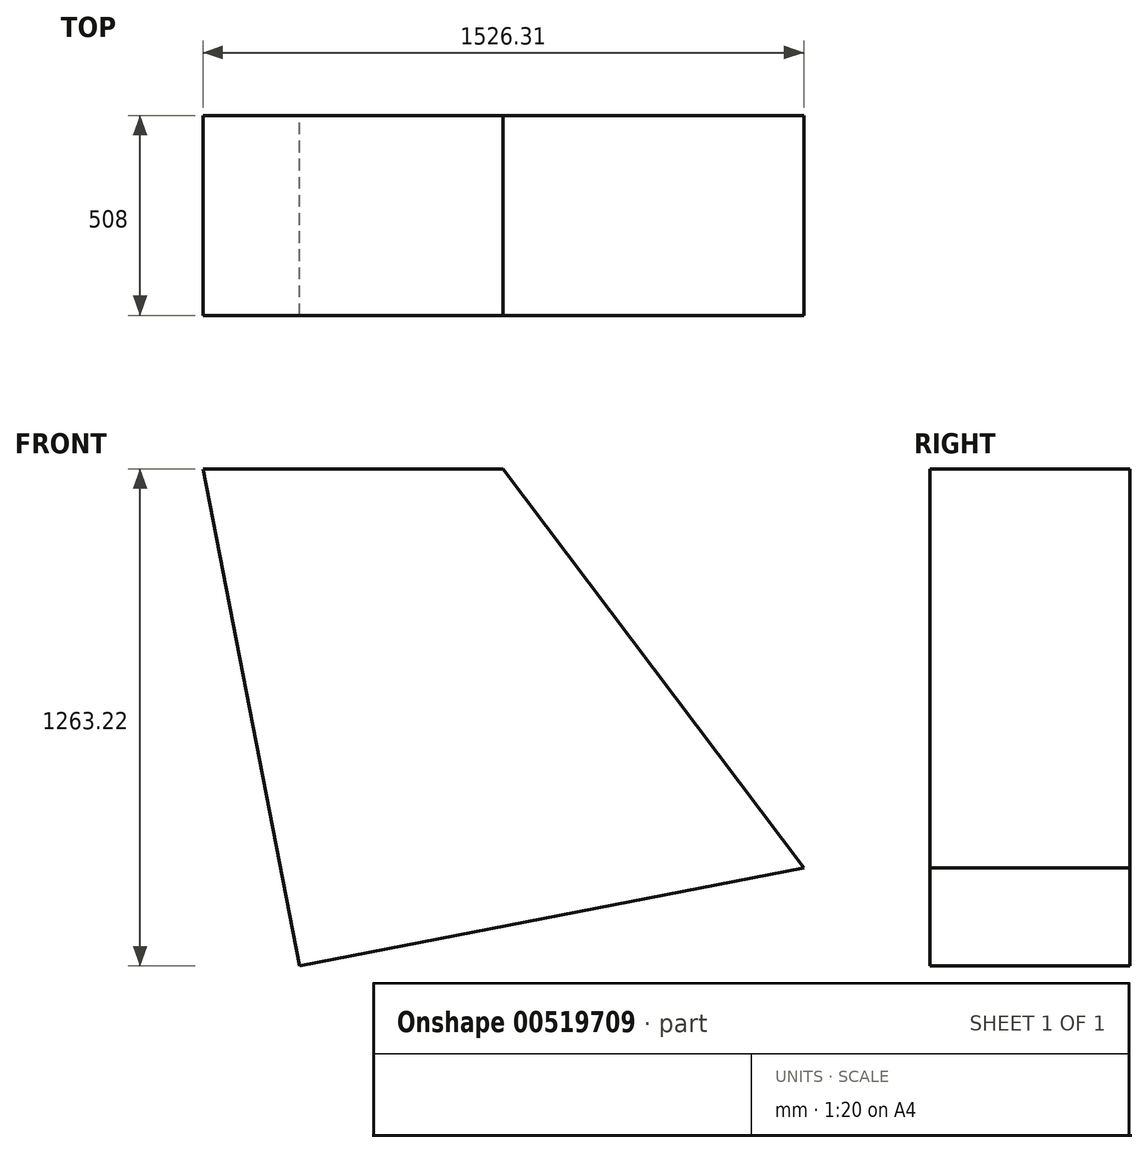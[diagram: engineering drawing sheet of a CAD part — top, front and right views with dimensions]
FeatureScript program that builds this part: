
annotation { "Feature Type Name" : "Feature", "Feature Type Description" : "" }
export const myFeature = defineFeature(function(context is Context, id is Id, definition is map)
    precondition{}
    {
        {
            var Q0;
            Q0=qCreatedBy(makeId("Front.planeOp"),FACE);
            var sketch = newSketch(context, id + "F0", { "sketchPlane" : qUnion([Q0])});
            skLineSegment(sketch, "E0", {"start": v(0, 53.86) * mm, "end": v(245.55, -1209.36) * mm});
            skLineSegment(sketch, "E1", {"start": v(0, 53.86) * mm, "end": v(762, 53.86) * mm});
            skLineSegment(sketch, "E2", {"start": v(762, 53.86) * mm, "end": v(1526.3, -960.4) * mm});
            skLineSegment(sketch, "E3", {"start": v(245.55, -1209.36) * mm, "end": v(1526.3, -960.4) * mm});
            skSolve(sketch);
        }
        {
            var Q0;
            Q0=makeQuery(id+"F0.imprint","IMPRINT",FACE,{"disambiguationData":[TD([[makeQuery(id+"F0.imprint","IMPRINT",EDGE,{"derivedFrom":sQuery(id+"F0.wireOp",EDGE,"E0")}),1.0]])]});
            extrude(context, id + "F1", {"entities" : qUnion([Q0]), "depth" : 508 * mm, "offsetDistance" : 25.4 * mm});
        }
    });
